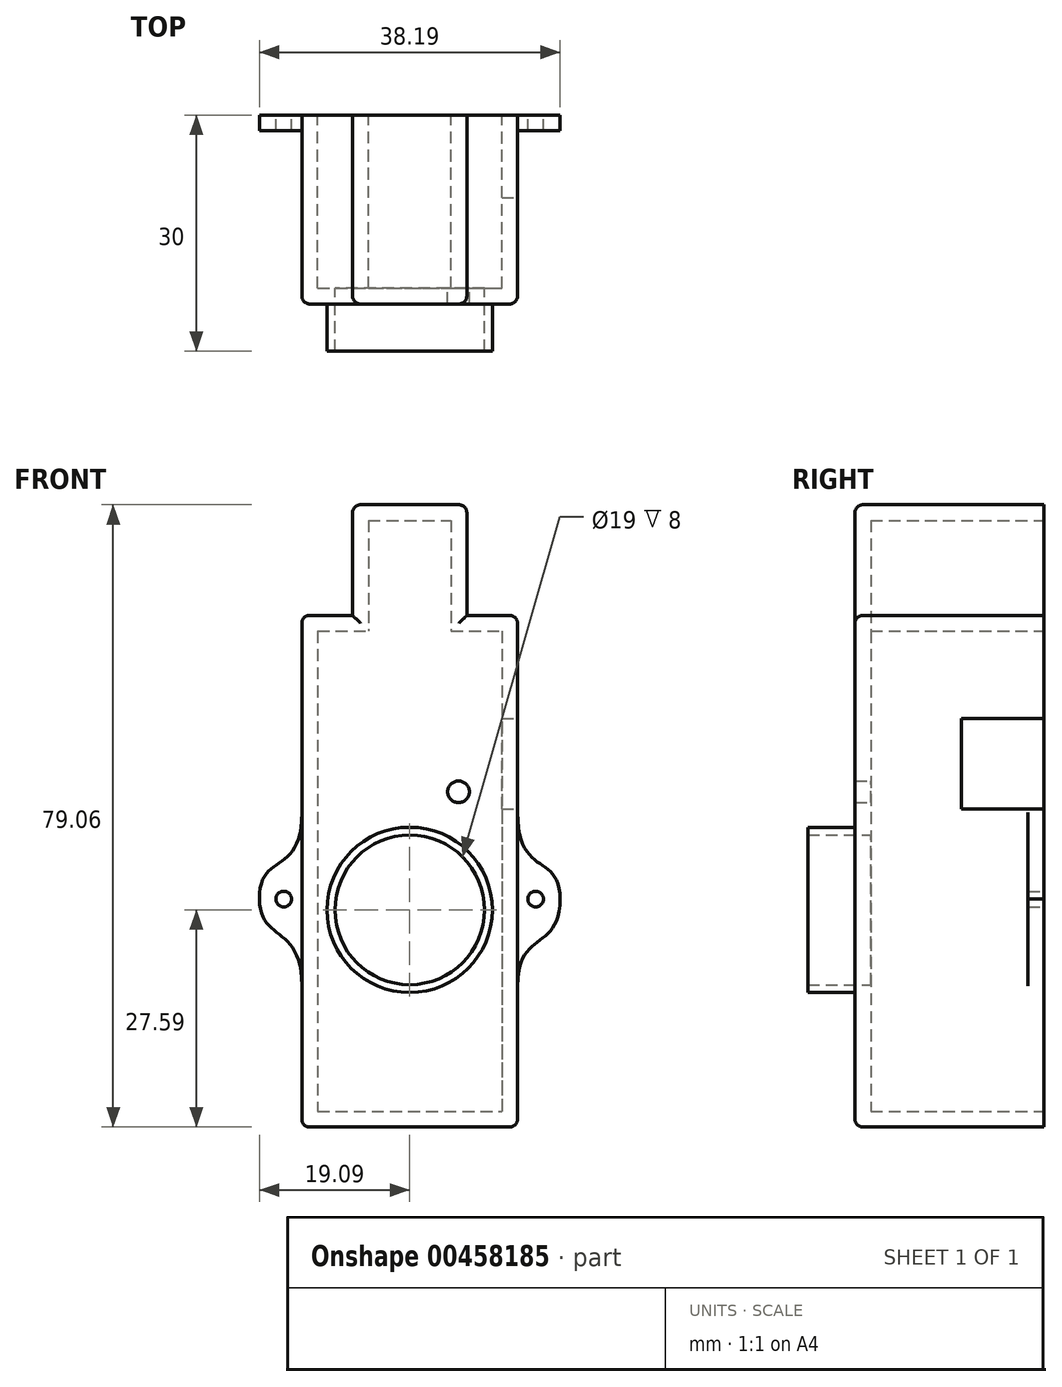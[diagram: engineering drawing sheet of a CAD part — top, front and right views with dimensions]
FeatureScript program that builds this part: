
annotation { "Feature Type Name" : "Feature", "Feature Type Description" : "" }
export const myFeature = defineFeature(function(context is Context, id is Id, definition is map)
    precondition{}
    {
        {
            var Q0;
            Q0=qCreatedBy(makeId("Front.planeOp"),FACE);
            var sketch = newSketch(context, id + "F0", { "sketchPlane" : qUnion([Q0])});
            skLineSegment(sketch, "E0.bottom", {"start": v(-13.7, 32.5) * mm, "end": v(13.7, 32.5) * mm});
            skLineSegment(sketch, "E0.top", {"start": v(-13.7, -32.5) * mm, "end": v(13.7, -32.5) * mm});
            skLineSegment(sketch, "E0.left", {"start": v(-13.7, 32.5) * mm, "end": v(-13.7, -32.5) * mm});
            skLineSegment(sketch, "E0.right", {"start": v(13.7, 32.5) * mm, "end": v(13.7, -32.5) * mm});
            skPoint(sketch, "E0.middle", {"position": v(0, 0) * mm});
            skLineSegment(sketch, "E1.bottom", {"start": v(-7.25, 46.56) * mm, "end": v(7.25, 46.56) * mm});
            skLineSegment(sketch, "E1.top", {"start": v(-7.25, 32.5) * mm, "end": v(7.25, 32.5) * mm});
            skLineSegment(sketch, "E1.left", {"start": v(-7.25, 46.56) * mm, "end": v(-7.25, 32.5) * mm});
            skLineSegment(sketch, "E1.right", {"start": v(7.25, 46.56) * mm, "end": v(7.25, 32.5) * mm});
            skPoint(sketch, "E1.middle", {"position": v(0, 39.53) * mm});
            skCircle(sketch, "E2", {"center": v(6.2, 10.1) * mm, "radius": 1.38 * mm});
            skCircle(sketch, "E3", {"center": v(-16, -3.54) * mm, "radius": 1 * mm});
            skCircle(sketch, "E4", {"center": v(16, -3.54) * mm, "radius": 1 * mm});
            skPoint(sketch, "E5", {"position": v(-13.7, 7.5) * mm});
            skFitSpline(sketch, "E6", {"points": [v(-19.1, -3.5) * mm, v(-13.7, 7.5) * mm], "startDerivative": vector(-0.03, 18.41) * mm, "endDerivative": vector(0, 24.9) * mm});
            skPoint(sketch, "E7", {"position": v(-13.7, -14.5) * mm});
            skFitSpline(sketch, "E8", {"points": [v(-19.1, -3.5) * mm, v(-13.7, -14.5) * mm], "startDerivative": vector(0.08, -16.69) * mm, "endDerivative": vector(0, -23.36) * mm});
            skPoint(sketch, "E9", {"position": v(13.7, 7.46) * mm});
            skPoint(sketch, "E10", {"position": v(13.7, -14.54) * mm});
            skFitSpline(sketch, "E11", {"points": [v(19.1, -3.54) * mm, v(13.7, 7.46) * mm], "startDerivative": vector(-0.21, 18.1) * mm, "endDerivative": vector(0, 25.12) * mm});
            skFitSpline(sketch, "E12", {"points": [v(19.1, -3.54) * mm, v(13.7, -14.54) * mm], "startDerivative": vector(-0.21, -20.2) * mm, "endDerivative": vector(0, -21.48) * mm});
            skCircle(sketch, "E13", {"center": v(0, -4.91) * mm, "radius": 9.5 * mm});
            skCircle(sketch, "E14", {"center": v(0, -4.91) * mm, "radius": 10.5 * mm});
            skSolve(sketch);
        }
        {
            var Q0;
            {var subQ2=sQuery(id+"F0.wireOp",EDGE,"E0.top");Q0=makeQuery(id+"F0.imprint","IMPRINT",FACE,{"disambiguationData":[TD([[makeQuery(id+"F0.imprint","IMPRINT",EDGE,{"derivedFrom":subQ2}),1.0]])]});}
            var Q1;
            Q1=makeQuery(id+"F0.imprint","IMPRINT",FACE,{"disambiguationData":[TD([[makeQuery(id+"F0.imprint","IMPRINT",EDGE,{"derivedFrom":sQuery(id+"F0.wireOp",EDGE,"E1.bottom")}),-1.0]])]});
            extrude(context, id + "F1", {"entities" : qUnion([Q0, Q1]), "depth" : 24 * mm});
        }
        {
            var Q0;
            Q0=makeQuery(id+"F1.opExtrude","CAP_FACE",FACE,{"disambiguationData":[OSD([sQuery(id+"F0.wireOp",EDGE,"E0.bottom"),sQuery(id+"F0.wireOp",EDGE,"E0.top"),sQuery(id+"F0.wireOp",EDGE,"E0.left"),sQuery(id+"F0.wireOp",EDGE,"E0.right"),sQuery(id+"F0.wireOp",EDGE,"E1.bottom"),sQuery(id+"F0.wireOp",EDGE,"E1.left"),sQuery(id+"F0.wireOp",EDGE,"E1.right"),sQuery(id+"F0.wireOp",EDGE,"E2"),sQuery(id+"F0.wireOp",EDGE,"3NyNIGW7-3qz9-oh3A-DnwY-PbWO1NzhsHBr")])],"isStart":true});
            shell(context, id + "F2", {"entities" : qUnion([Q0]), "thickness" : 2 * mm});
        }
        {
            var Q0;
            Q0=makeQuery(id+"F0.imprint","IMPRINT",FACE,{"disambiguationData":[TD([[makeQuery(id+"F0.imprint","IMPRINT",EDGE,{"derivedFrom":sQuery(id+"F0.wireOp",EDGE,"E13")}),-1.0]])]});
            extrude(context, id + "F3", {"entities" : qUnion([Q0]), "operationType" : NewBodyOperationType.ADD, "depth" : 30 * mm});
        }
        {
            var Q0;
            Q0=makeQuery(id+"F0.imprint","IMPRINT",FACE,{"disambiguationData":[TD([[makeQuery(id+"F0.imprint","IMPRINT",EDGE,{"derivedFrom":sQuery(id+"F0.wireOp",EDGE,"E3")}),-1.0]])]});
            var Q1;
            Q1=makeQuery(id+"F0.imprint","IMPRINT",FACE,{"disambiguationData":[TD([[makeQuery(id+"F0.imprint","IMPRINT",EDGE,{"derivedFrom":sQuery(id+"F0.wireOp",EDGE,"E4")}),-1.0]])]});
            extrude(context, id + "F4", {"entities" : qUnion([Q0, Q1]), "operationType" : NewBodyOperationType.ADD, "depth" : 2 * mm});
        }
        {
            var Q0;
            Q0=makeQuery(id+"F1.opExtrude","SWEPT_EDGE",EDGE,{"disambiguationData":[OSD([sQuery(id+"F0.wireOp",EDGE,"E0.bottom"),sQuery(id+"F0.wireOp",EDGE,"E0.right")])]});
            var Q1;
            Q1=makeQuery(id+"F1.opExtrude","SWEPT_EDGE",EDGE,{"disambiguationData":[OSD([sQuery(id+"F0.wireOp",EDGE,"E0.bottom"),sQuery(id+"F0.wireOp",EDGE,"E0.left")])]});
            var Q2;
            Q2=makeQuery(id+"F1.opExtrude","SWEPT_EDGE",EDGE,{"disambiguationData":[OSD([sQuery(id+"F0.wireOp",EDGE,"E0.top"),sQuery(id+"F0.wireOp",EDGE,"E0.left")])]});
            var Q3;
            Q3=makeQuery(id+"F1.opExtrude","SWEPT_EDGE",EDGE,{"disambiguationData":[OSD([sQuery(id+"F0.wireOp",EDGE,"E0.top"),sQuery(id+"F0.wireOp",EDGE,"E0.right")])]});
            var Q4;
            Q4=makeQuery(id+"F1.opExtrude","SWEPT_EDGE",EDGE,{"disambiguationData":[OSD([sQuery(id+"F0.wireOp",EDGE,"E1.bottom"),sQuery(id+"F0.wireOp",EDGE,"E1.right")])]});
            var Q5;
            Q5=makeQuery(id+"F1.opExtrude","SWEPT_EDGE",EDGE,{"disambiguationData":[OSD([sQuery(id+"F0.wireOp",EDGE,"E1.bottom"),sQuery(id+"F0.wireOp",EDGE,"E1.left")])]});
            var Q6;
            Q6=makeQuery(id+"F1.opExtrude","CAP_EDGE",EDGE,{"disambiguationData":[OSD([sQuery(id+"F0.wireOp",EDGE,"E1.right")])],"isStart":false});
            var Q7;
            Q7=makeQuery(id+"F1.opExtrude","CAP_EDGE",EDGE,{"disambiguationData":[OSD([sQuery(id+"F0.wireOp",EDGE,"E1.left")])],"isStart":false});
            var Q8;
            Q8=makeQuery(id+"F1.opExtrude","CAP_EDGE",EDGE,{"disambiguationData":[OSD([sQuery(id+"F0.wireOp",EDGE,"E0.left")])],"isStart":false});
            var Q9;
            Q9=makeQuery(id+"F1.opExtrude","CAP_EDGE",EDGE,{"disambiguationData":[OSD([sQuery(id+"F0.wireOp",EDGE,"E0.right")])],"isStart":false});
            var Q10;
            Q10=makeQuery(id+"F1.opExtrude","CAP_EDGE",EDGE,{"disambiguationData":[OSD([sQuery(id+"F0.wireOp",EDGE,"E0.top")])],"isStart":false});
            var Q11;
            {var subQ0=sQuery(id+"F0.wireOp",EDGE,"E0.bottom");Q11=makeQuery(id+"F1.opExtrude","CAP_EDGE",EDGE,{"disambiguationData":[OSD([subQ0]),TDD([makeQuery(id+"F0.imprint","IMPRINT",EDGE,{"disambiguationData":[TD([[makeQuery(id+"F0.imprint","INTERSECT",VERTEX,{"derivedFrom":[subQ0,sQuery(id+"F0.wireOp",EDGE,"E0.left")]}),-1.0]])],"derivedFrom":subQ0})])],"isStart":false});}
            var Q12;
            {var subQ0=sQuery(id+"F0.wireOp",EDGE,"E0.bottom");Q12=makeQuery(id+"F1.opExtrude","CAP_EDGE",EDGE,{"disambiguationData":[OSD([subQ0]),TDD([makeQuery(id+"F0.imprint","IMPRINT",EDGE,{"disambiguationData":[TD([[makeQuery(id+"F0.imprint","INTERSECT",VERTEX,{"derivedFrom":[subQ0,sQuery(id+"F0.wireOp",EDGE,"E0.right")]}),1.0]])],"derivedFrom":subQ0})])],"isStart":false});}
            var Q13;
            Q13=makeQuery(id+"F1.opExtrude","CAP_EDGE",EDGE,{"disambiguationData":[OSD([sQuery(id+"F0.wireOp",EDGE,"E1.bottom")])],"isStart":false});
            fillet(context, id + "F5", {"entities" : qUnion([Q0, Q1, Q2, Q3, Q4, Q5, Q6, Q7, Q8, Q9, Q10, Q11, Q12, Q13]), "radius" : 1 * mm, "tangentPropagation" : true, "allowEdgeOverflow" : false});
        }
        {
            var Q0;
            Q0=makeQuery(id+"F1.opExtrude","CAP_FACE",FACE,{"disambiguationData":[OSD([sQuery(id+"F0.wireOp",EDGE,"E0.bottom"),sQuery(id+"F0.wireOp",EDGE,"E0.top"),sQuery(id+"F0.wireOp",EDGE,"E0.left"),sQuery(id+"F0.wireOp",EDGE,"E0.right"),sQuery(id+"F0.wireOp",EDGE,"E1.bottom"),sQuery(id+"F0.wireOp",EDGE,"E1.left"),sQuery(id+"F0.wireOp",EDGE,"E1.right"),sQuery(id+"F0.wireOp",EDGE,"E2"),sQuery(id+"F0.wireOp",EDGE,"E14")])],"isStart":true});
            var sketch = newSketch(context, id + "F6", { "sketchPlane" : qUnion([Q0])});
            skCircle(sketch, "E15.0", {"center": v(-6.2, 10.1) * mm, "radius": 3.38 * mm});
            skSolve(sketch);
        }
        {
            var Q0;
            Q0 = qSketchRegion(id + "F6", true);
            var Q1;
            {var subQ0=sQuery(id+"F0.wireOp",EDGE,"E14");var subQ1=sQuery(id+"F0.wireOp",EDGE,"E2");var subQ2=sQuery(id+"F0.wireOp",EDGE,"E1.right");var subQ3=sQuery(id+"F0.wireOp",EDGE,"E1.left");var subQ4=sQuery(id+"F0.wireOp",EDGE,"E1.bottom");var subQ5=sQuery(id+"F0.wireOp",EDGE,"E0.right");var subQ6=sQuery(id+"F0.wireOp",EDGE,"E0.left");var subQ7=sQuery(id+"F0.wireOp",EDGE,"E0.top");var subQ8=sQuery(id+"F0.wireOp",EDGE,"E0.bottom");Q1=makeQuery(id+"F2.opShell","OFFSET_FACE",FACE,{"disambiguationData":[OSD([subQ8,subQ7,subQ6,subQ5,subQ4,subQ3,subQ2,subQ1,subQ0]),TDD([makeQuery(id+"F1.opExtrude","CAP_FACE",FACE,{"disambiguationData":[OSD([subQ8,subQ7,subQ6,subQ5,subQ4,subQ3,subQ2,subQ1,subQ0])],"isStart":false})]),OD(0.0)]});}
            extrude(context, id + "F7", {"entities" : qUnion([Q0]), "operationType" : NewBodyOperationType.REMOVE, "endBound" : BoundingType.UP_TO_SURFACE, "oppositeDirection" : true, "endBoundEntityFace" : qUnion([Q1]), "depth" : 25 * mm});
        }
        {
            var Q0;
            {var subQ0=sQuery(id+"F0.wireOp",EDGE,"E14");var subQ1=sQuery(id+"F0.wireOp",EDGE,"E2");var subQ2=sQuery(id+"F0.wireOp",EDGE,"E1.right");var subQ3=sQuery(id+"F0.wireOp",EDGE,"E1.left");var subQ4=sQuery(id+"F0.wireOp",EDGE,"E1.bottom");var subQ5=sQuery(id+"F0.wireOp",EDGE,"E0.right");var subQ6=sQuery(id+"F0.wireOp",EDGE,"E0.left");var subQ7=sQuery(id+"F0.wireOp",EDGE,"E0.top");var subQ8=sQuery(id+"F0.wireOp",EDGE,"E0.bottom");Q0=makeQuery(id+"F3.boolean.opBoolean","MERGE",FACE,{"derivedFrom":[makeQuery(id+"F2.opShell","OFFSET_FACE",FACE,{"disambiguationData":[OSD([subQ8,subQ7,subQ6,subQ5,subQ4,subQ3,subQ2,subQ1,subQ0]),TDD([makeQuery(id+"F1.opExtrude","CAP_FACE",FACE,{"disambiguationData":[OSD([subQ8,subQ7,subQ6,subQ5,subQ4,subQ3,subQ2,subQ1,subQ0])],"isStart":true})])]}),makeQuery(id+"F3.opExtrude","CAP_FACE",FACE,{"disambiguationData":[OSD([sQuery(id+"F0.wireOp",EDGE,"E13"),subQ0])],"isStart":true})]});}
            var sketch = newSketch(context, id + "F8", { "sketchPlane" : qUnion([Q0])});
            skArc(sketch, "E16.0", {"start": v(11.7, -9.31) * mm, "mid": v(0, -17.41) * mm, "end": v(-11.7, -9.31) * mm});
            skArc(sketch, "E17.0", {"start": v(-11.7, -0.5) * mm, "mid": v(0, 7.6) * mm, "end": v(11.7, -0.5) * mm});
            skLineSegment(sketch, "E18", {"start": v(-11.7, -9.31) * mm, "end": v(-11.7, -0.5) * mm});
            skLineSegment(sketch, "E19", {"start": v(11.7, -9.31) * mm, "end": v(11.7, -0.5) * mm});
            skSolve(sketch);
        }
        {
            var Q0;
            Q0 = qSketchRegion(id + "F8", true);
            var Q1;
            {var subQ0=sQuery(id+"F0.wireOp",EDGE,"E14");var subQ1=sQuery(id+"F0.wireOp",EDGE,"E2");var subQ2=sQuery(id+"F0.wireOp",EDGE,"E1.right");var subQ3=sQuery(id+"F0.wireOp",EDGE,"E1.left");var subQ4=sQuery(id+"F0.wireOp",EDGE,"E1.bottom");var subQ5=sQuery(id+"F0.wireOp",EDGE,"E0.right");var subQ6=sQuery(id+"F0.wireOp",EDGE,"E0.left");var subQ7=sQuery(id+"F0.wireOp",EDGE,"E0.top");var subQ8=sQuery(id+"F0.wireOp",EDGE,"E0.bottom");Q1=makeQuery(id+"F2.opShell","OFFSET_FACE",FACE,{"disambiguationData":[OSD([subQ8,subQ7,subQ6,subQ5,subQ4,subQ3,subQ2,subQ1,subQ0]),TDD([makeQuery(id+"F1.opExtrude","CAP_FACE",FACE,{"disambiguationData":[OSD([subQ8,subQ7,subQ6,subQ5,subQ4,subQ3,subQ2,subQ1,subQ0])],"isStart":false})]),OD(1.0)]});}
            extrude(context, id + "F9", {"entities" : qUnion([Q0]), "operationType" : NewBodyOperationType.REMOVE, "endBound" : BoundingType.UP_TO_SURFACE, "oppositeDirection" : true, "endBoundEntityFace" : qUnion([Q1]), "depth" : 25 * mm});
        }
        {
            var Q0;
            Q0=makeQuery(id+"F1.opExtrude","SWEPT_FACE",FACE,{"disambiguationData":[OSD([sQuery(id+"F0.wireOp",EDGE,"E0.right")])]});
            var sketch = newSketch(context, id + "F10", { "sketchPlane" : qUnion([Q0])});
            skLineSegment(sketch, "E20", {"start": v(0, 19.4) * mm, "end": v(-10.5, 19.4) * mm});
            skLineSegment(sketch, "E21", {"start": v(-10.5, 19.4) * mm, "end": v(-10.5, 7.9) * mm});
            skLineSegment(sketch, "E22", {"start": v(-10.5, 7.9) * mm, "end": v(0, 7.9) * mm});
            skSolve(sketch);
        }
        {
            var Q0;
            {var subQ0=sQuery(id+"F10.wireOp",EDGE,"E20");Q0=makeQuery(id+"F10.imprint","IMPRINT",FACE,{"disambiguationData":[TD([[makeQuery(id+"F10.imprint","IMPRINT",EDGE,{"derivedFrom":subQ0}),1.0]])]});}
            extrude(context, id + "F11", {"entities" : qUnion([Q0]), "operationType" : NewBodyOperationType.REMOVE, "endBound" : BoundingType.UP_TO_NEXT, "oppositeDirection" : true, "depth" : 25 * mm});
        }
    });
